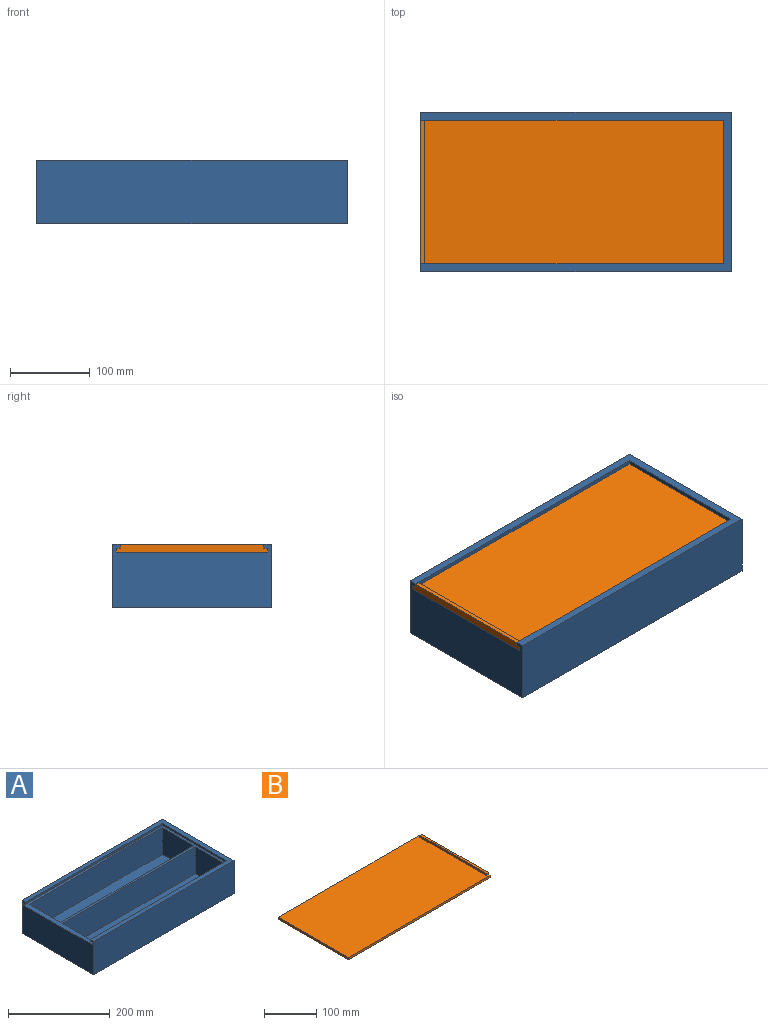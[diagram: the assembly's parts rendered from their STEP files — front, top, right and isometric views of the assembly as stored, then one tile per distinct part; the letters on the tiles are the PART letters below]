
ASSEMBLY  parts=2 mates=1
PART A: 24 faces, bbox 390x200x80 mm
  f0: plane 87.5x65mm, normal (-1,0,0), area 5687.5mm2, adj f5,f9,f18,f19
  f1: plane 87.5x65mm, normal (-1,0,0), area 5687.5mm2, adj f8,f10,f11,f19
  f2: plane 87.5x65mm, normal (1,0,0), area 5687.5mm2, adj f8,f10,f11,f19
  f3: plane 390x200mm, normal (0,0,1), area 9600mm2, adj f4,f7,f12,f13,f14,f15,f17
  f4: plane 380x5mm, normal (0,-1,0), area 1900mm2, adj f3,f14,f17,f21
  f5: plane 370x65mm, normal (0,-1,0), area 24050mm2, adj f0,f6,f18,f19
  f6: plane 87.5x65mm, normal (1,0,0), area 5687.5mm2, adj f5,f9,f18,f19
  f7: plane 380x5mm, normal (0,1,0), area 1900mm2, adj f3,f14,f17,f21
  f8: plane 370x65mm, normal (0,1,0), area 24050mm2, adj f1,f2,f11,f19
  f9: plane 370x65mm, normal (0,1,0), area 24050mm2, adj f0,f6,f18,f19
  f10: plane 370x65mm, normal (0,-1,0), area 24050mm2, adj f1,f2,f11,f19
  f11: plane 370x87.5mm, normal (0,0,1), area 32375mm2, adj f1,f2,f8,f10
  f12: plane 200x80mm, normal (1,0,0), area 16000mm2, adj f3,f13,f15,f16
  f13: plane 390x80mm, normal (0,1,0), area 31200mm2, adj f3,f12,f14,f16
  f14: plane 200x80mm, normal (-1,0,0), area 14150mm2, adj f3,f4,f7,f13,f15,f16,f19,f20
  f15: plane 390x80mm, normal (0,-1,0), area 31200mm2, adj f3,f12,f14,f16
  f16: plane 390x200mm, normal (0,0,-1), area 78000mm2, adj f12,f13,f14,f15
  f17: plane 180x5mm, normal (-1,0,0), area 900mm2, adj f3,f4,f7,f21
  f18: plane 370x87.5mm, normal (0,0,1), area 32375mm2, adj f0,f5,f6,f9
  f19: plane 385x190mm, normal (0,0,1), area 8400mm2, adj f0,f1,f2,f5,f6,f8,f9,f10
  f20: plane 385x5mm, normal (0,1,0), area 1925mm2, adj f14,f19,f21,f23
  f21: plane 385x190mm, normal (0,0,-1), area 4750mm2, adj f4,f7,f14,f17,f20,f22,f23
  f22: plane 385x5mm, normal (0,-1,0), area 1925mm2, adj f14,f19,f21,f23
  f23: plane 190x5mm, normal (-1,0,0), area 950mm2, adj f19,f20,f21,f22
PART B: 10 faces, bbox 385x190x10 mm
  f0: plane 190x10mm, normal (1,0,0), area 1850mm2, adj f1,f3,f5,f6,f7,f8,f9
  f1: plane 385x5mm, normal (0,1,0), area 1925mm2, adj f0,f4,f5,f6
  f2: plane 180x5mm, normal (-1,0,0), area 900mm2, adj f5,f7,f8,f9
  f3: plane 385x5mm, normal (0,-1,0), area 1925mm2, adj f0,f4,f5,f6
  f4: plane 190x5mm, normal (-1,0,0), area 950mm2, adj f1,f3,f5,f6
  f5: plane 385x190mm, normal (0,0,1), area 72250mm2, adj f0,f1,f2,f3,f4,f8,f9
  f6: plane 385x190mm, normal (0,0,-1), area 73150mm2, adj f0,f1,f3,f4
  f7: plane 180x5mm, normal (0,0,1), area 900mm2, adj f0,f2,f8,f9
  f8: plane 5x5mm, normal (0,-1,0), area 25mm2, adj f0,f2,f5,f7
  f9: plane 5x5mm, normal (0,1,0), area 25mm2, adj f0,f2,f5,f7
PLACE A t=(121.76,-360.02,-299.34)mm fixed
PLACE B rot(axis=(0,0,1),180deg) t=(119.26,-360.02,-229.34)mm
MATE slider B.f4 <-> A.f14  axis (1,0,0) through (311.76,-455.02,-224.34)mm
